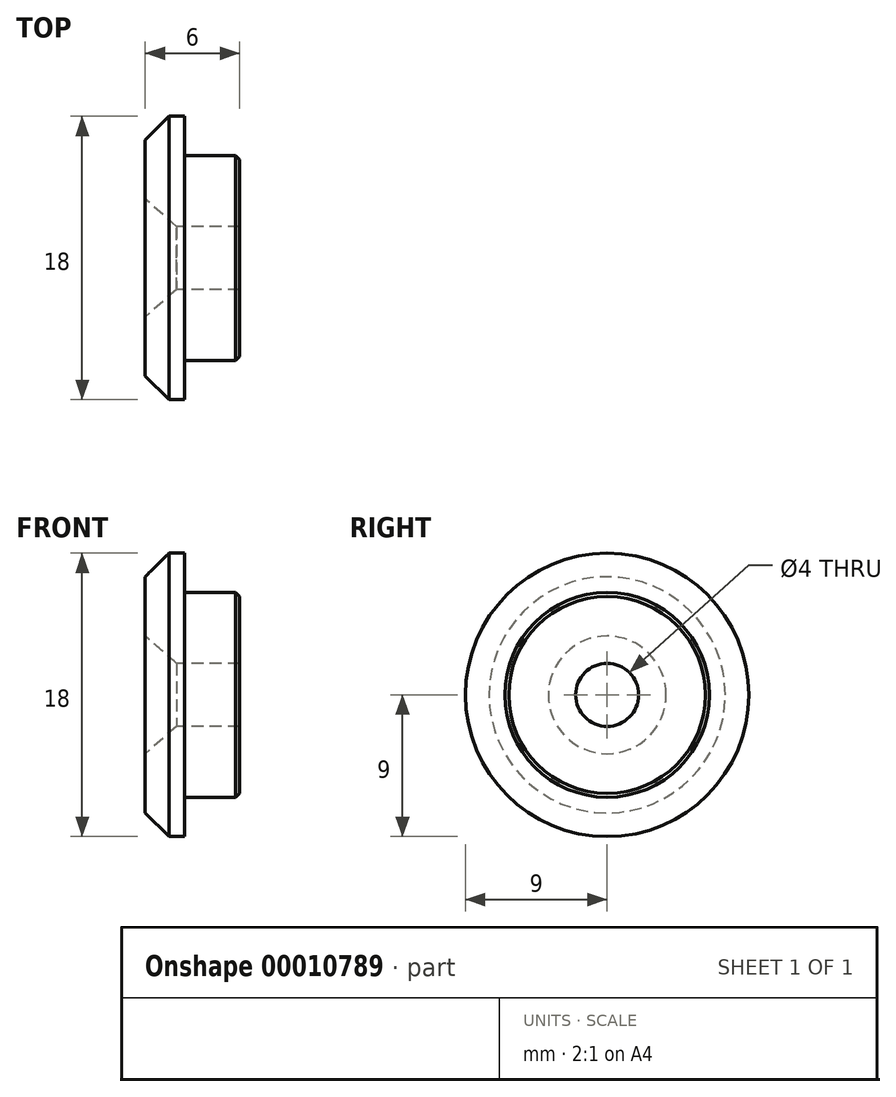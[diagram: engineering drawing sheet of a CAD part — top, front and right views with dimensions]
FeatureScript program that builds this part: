
annotation { "Feature Type Name" : "Feature", "Feature Type Description" : "" }
export const myFeature = defineFeature(function(context is Context, id is Id, definition is map)
    precondition{}
    {
        {
            var Q0;
            Q0=qCreatedBy(makeId("Right.planeOp"),FACE);
            var sketch = newSketch(context, id + "F0", { "sketchPlane" : qUnion([Q0])});
            skCircle(sketch, "E0", {"center": v(0, 0) * mm, "radius": 6.5 * mm});
            skCircle(sketch, "E1", {"center": v(0, 0) * mm, "radius": 2 * mm});
            skSolve(sketch);
        }
        {
            var Q0;
            Q0 = qSketchRegion(id + "F0", true);
            extrude(context, id + "F1", {"entities" : qUnion([Q0]), "depth" : 3.5 * mm});
        }
        {
            var Q0;
            Q0=makeQuery(id+"F1.opExtrude","CAP_FACE",FACE,{"disambiguationData":[OSD([sQuery(id+"F0.wireOp",EDGE,"E0"),sQuery(id+"F0.wireOp",EDGE,"E1")])],"isStart":true});
            var sketch = newSketch(context, id + "F2", { "sketchPlane" : qUnion([Q0])});
            skCircle(sketch, "E2.0", {"center": v(0, 0) * mm, "radius": 2 * mm});
            skCircle(sketch, "E3", {"center": v(0, 0) * mm, "radius": 9 * mm});
            skSolve(sketch);
        }
        {
            var Q0;
            Q0 = qSketchRegion(id + "F2", true);
            extrude(context, id + "F3", {"entities" : qUnion([Q0]), "operationType" : NewBodyOperationType.ADD, "depth" : 2.5 * mm});
        }
        {
            var Q0;
            Q0=makeQuery(id+"F3.opExtrude","CAP_EDGE",EDGE,{"disambiguationData":[OSD([sQuery(id+"F2.wireOp",EDGE,"E3")])],"isStart":false});
            chamfer(context, id + "F4", {"entities" : qUnion([Q0]), "chamferType" : ChamferType.OFFSET_ANGLE, "width" : 1.5 * mm, "oppositeDirection" : false, "angle" : 45 * degree, "tangentPropagation" : true});
        }
        {
            var Q0;
            Q0=makeQuery(id+"F3.opExtrude","CAP_EDGE",EDGE,{"disambiguationData":[OSD([sQuery(id+"F2.wireOp",EDGE,"E2.0")])],"isStart":false});
            chamfer(context, id + "F5", {"entities" : qUnion([Q0]), "chamferType" : ChamferType.OFFSET_ANGLE, "width" : 2 * mm, "oppositeDirection" : false, "angle" : 41 * degree, "tangentPropagation" : true});
        }
        {
            var Q0;
            Q0=makeQuery(id+"F1.opExtrude","CAP_EDGE",EDGE,{"disambiguationData":[OSD([sQuery(id+"F0.wireOp",EDGE,"E0")])],"isStart":false});
            chamfer(context, id + "F6", {"entities" : qUnion([Q0]), "width" : .25 * mm, "tangentPropagation" : true});
        }
    });
